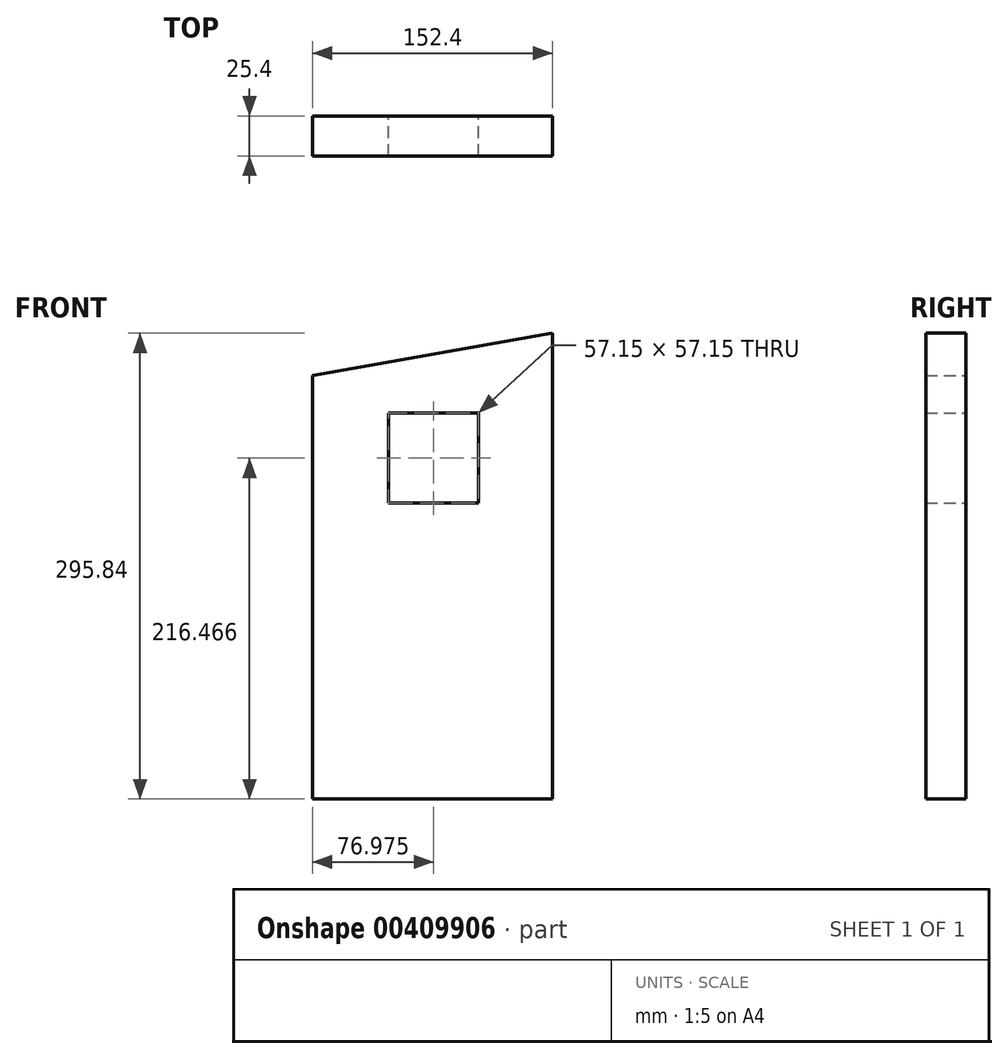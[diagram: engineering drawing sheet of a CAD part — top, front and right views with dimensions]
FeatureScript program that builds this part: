
annotation { "Feature Type Name" : "Feature", "Feature Type Description" : "" }
export const myFeature = defineFeature(function(context is Context, id is Id, definition is map)
    precondition{}
    {
        {
            var Q0;
            Q0=qCreatedBy(makeId("Front.planeOp"),FACE);
            var sketch = newSketch(context, id + "F0", { "sketchPlane" : qUnion([Q0])});
            skLineSegment(sketch, "E0.bottom", {"start": v(-105.55, 148) * mm, "end": v(46.85, 148) * mm});
            skLineSegment(sketch, "E0.top", {"start": v(-105.55, -156.8) * mm, "end": v(46.85, -156.8) * mm});
            skLineSegment(sketch, "E0.left", {"start": v(-105.55, 148) * mm, "end": v(-105.55, -156.8) * mm});
            skLineSegment(sketch, "E0.right", {"start": v(46.85, 148) * mm, "end": v(46.85, -156.8) * mm});
            skSolve(sketch);
        }
        {
            var Q0;
            Q0 = qSketchRegion(id + "F0", true);
            extrude(context, id + "F1", {"entities" : qUnion([Q0]), "depth" : 25.4 * mm});
        }
        {
            var Q0;
            Q0=makeQuery(id+"F1.opExtrude","SWEPT_EDGE",EDGE,{"disambiguationData":[OSD([sQuery(id+"F0.wireOp",EDGE,"E0.bottom"),sQuery(id+"F0.wireOp",EDGE,"E0.left")])]});
            chamfer(context, id + "F2", {"entities" : qUnion([Q0]), "chamferType" : ChamferType.OFFSET_ANGLE, "width" : 203.2 * mm, "oppositeDirection" : true, "angle" : 10 * degree, "tangentPropagation" : true});
        }
        {
            var Q0;
            Q0 = qSketchRegion(id + "F0", true);
            var sketch = newSketch(context, id + "F3", { "sketchPlane" : qUnion([Q0])});
            skLineSegment(sketch, "E1.bottom", {"start": v(-57.15, 88.25) * mm, "end": v(0, 88.25) * mm});
            skLineSegment(sketch, "E1.top", {"start": v(-57.15, 31.1) * mm, "end": v(0, 31.1) * mm});
            skLineSegment(sketch, "E1.left", {"start": v(-57.15, 88.25) * mm, "end": v(-57.15, 31.1) * mm});
            skLineSegment(sketch, "E1.right", {"start": v(0, 88.25) * mm, "end": v(0, 31.1) * mm});
            skSolve(sketch);
        }
        {
            var Q0;
            Q0 = qSketchRegion(id + "F3", true);
            extrude(context, id + "F4", {"entities" : qUnion([Q0]), "operationType" : NewBodyOperationType.REMOVE, "endBound" : BoundingType.UP_TO_NEXT, "depth" : 25.4 * mm});
        }
    });
